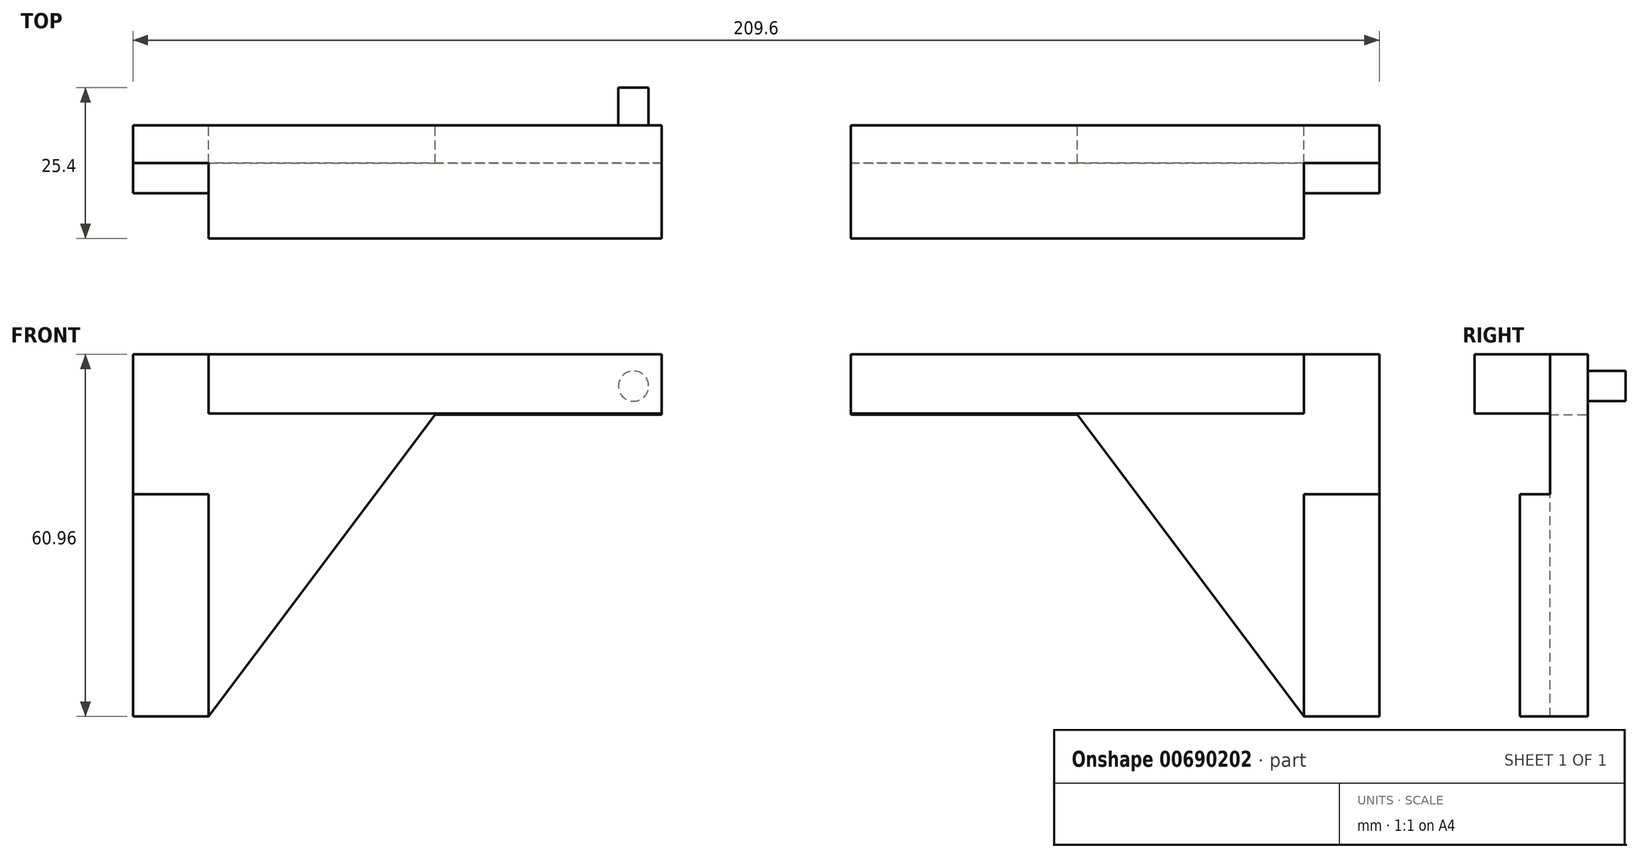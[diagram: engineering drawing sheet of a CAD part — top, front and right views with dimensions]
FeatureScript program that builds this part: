
annotation { "Feature Type Name" : "Feature", "Feature Type Description" : "" }
export const myFeature = defineFeature(function(context is Context, id is Id, definition is map)
    precondition{}
    {
        {
            var Q0;
            Q0=qCreatedBy(makeId("Front.planeOp"),FACE);
            var sketch = newSketch(context, id + "F0", { "sketchPlane" : qUnion([Q0])});
            skLineSegment(sketch, "E0.bottom", {"start": v(-92.1, -0.08) * mm, "end": v(-104.8, -0.08) * mm});
            skLineSegment(sketch, "E0.top", {"start": v(-92.1, 60.88) * mm, "end": v(-104.8, 60.88) * mm});
            skLineSegment(sketch, "E0.left", {"start": v(-92.1, -0.08) * mm, "end": v(-92.1, 60.88) * mm});
            skLineSegment(sketch, "E0.right", {"start": v(-104.8, -0.08) * mm, "end": v(-104.8, 60.88) * mm});
            skPoint(sketch, "E0.middle", {"position": v(-98.45, 30.4) * mm});
            skLineSegment(sketch, "E1", {"start": v(-92.1, 60.88) * mm, "end": v(-15.9, 60.88) * mm});
            skLineSegment(sketch, "E2.0", {"start": v(-92.1, 50.72) * mm, "end": v(-15.9, 50.72) * mm});
            skLineSegment(sketch, "E3", {"start": v(-15.9, 60.88) * mm, "end": v(-15.9, 50.72) * mm});
            skLineSegment(sketch, "E4", {"start": v(-92.1, -0.08) * mm, "end": v(-54, 50.72) * mm});
            skSolve(sketch);
        }
        {
            var Q0;
            Q0 = qSketchRegion(id + "F0", true);
            extrude(context, id + "F1", {"entities" : qUnion([Q0]), "depth" : 6.35 * mm, "offsetDistance" : 25.4 * mm});
        }
        {
            var Q0;
            Q0=makeQuery(id+"F1.opExtrude","CAP_FACE",FACE,{"disambiguationData":[OSD([sQuery(id+"F0.wireOp",EDGE,"E0.bottom"),sQuery(id+"F0.wireOp",EDGE,"E0.top"),sQuery(id+"F0.wireOp",EDGE,"E0.right"),sQuery(id+"F0.wireOp",EDGE,"E1"),sQuery(id+"F0.wireOp",EDGE,"E2.0"),sQuery(id+"F0.wireOp",EDGE,"E3"),sQuery(id+"F0.wireOp",EDGE,"E4")])],"isStart":false});
            var sketch = newSketch(context, id + "F2", { "sketchPlane" : qUnion([Q0])});
            skLineSegment(sketch, "E5.bottom", {"start": v(-104.8, -0.08) * mm, "end": v(-92.1, -0.08) * mm});
            skLineSegment(sketch, "E5.top", {"start": v(-104.8, 37.36) * mm, "end": v(-92.1, 37.36) * mm});
            skLineSegment(sketch, "E5.left", {"start": v(-104.8, -0.08) * mm, "end": v(-104.8, 37.36) * mm});
            skLineSegment(sketch, "E5.right", {"start": v(-92.1, -0.08) * mm, "end": v(-92.1, 37.36) * mm});
            skSolve(sketch);
        }
        {
            var Q0;
            Q0=makeQuery(id+"F2.imprint","IMPRINT",FACE,{"disambiguationData":[TD([[makeQuery(id+"F2.imprint","IMPRINT",EDGE,{"derivedFrom":sQuery(id+"F2.wireOp",EDGE,"E5.bottom")}),-1.0]])]});
            extrude(context, id + "F3", {"entities" : qUnion([Q0]), "operationType" : NewBodyOperationType.ADD, "depth" : 5.08 * mm, "offsetDistance" : 25.4 * mm});
        }
        {
            var Q0;
            {var subQ5=sQuery(id+"F0.wireOp",EDGE,"E1");Q0=makeQuery(id+"F0.imprint","IMPRINT",FACE,{"disambiguationData":[TD([[makeQuery(id+"F0.imprint","IMPRINT",EDGE,{"derivedFrom":subQ5}),-1.0]])]});}
            var sketch = newSketch(context, id + "F4", { "sketchPlane" : qUnion([Q0])});
            skCircle(sketch, "E6", {"center": v(-20.63, 55.53) * mm, "radius": 2.54 * mm});
            skSolve(sketch);
        }
        {
            var Q0;
            Q0=makeQuery(id+"F4.imprint","IMPRINT",FACE,{"disambiguationData":[TD([[makeQuery(id+"F4.imprint","IMPRINT",EDGE,{"derivedFrom":sQuery(id+"F4.wireOp",EDGE,"E6")}),1.0]])]});
            var Q1;
            Q1=sQuery(id+"F4.wireOp",EDGE,"E6");
            extrude(context, id + "F5", {"entities" : qUnion([Q0]), "surfaceEntities" : qUnion([Q1]), "oppositeDirection" : true, "depth" : 6.35 * mm, "offsetDistance" : 25.4 * mm});
        }
        {
            var Q0;
            Q0=makeQuery(id+"F1.opExtrude","SWEPT_BODY",BODY,{"disambiguationData":[OSD([sQuery(id+"F0.wireOp",EDGE,"E0.bottom"),sQuery(id+"F0.wireOp",EDGE,"E0.top"),sQuery(id+"F0.wireOp",EDGE,"E0.right"),sQuery(id+"F0.wireOp",EDGE,"E1"),sQuery(id+"F0.wireOp",EDGE,"E2.0"),sQuery(id+"F0.wireOp",EDGE,"E3"),sQuery(id+"F0.wireOp",EDGE,"E4")])]});
            transform(context, id + "F6", {"entities" : qUnion([Q0]), "transformType" : TransformType.TRANSLATION_3D, "dx" : 163.83 * mm, "dy" : -4.57 * mm, "dz" : -13.72 * mm, "makeCopy" : true});
        }
        {
            var Q0;
            Q0=makeQuery(id+"F6.opPattern","COPY",BODY,{"derivedFrom":makeQuery(id+"F1.opExtrude","SWEPT_BODY",BODY,{"disambiguationData":[OSD([sQuery(id+"F0.wireOp",EDGE,"E0.bottom"),sQuery(id+"F0.wireOp",EDGE,"E0.top"),sQuery(id+"F0.wireOp",EDGE,"E0.right"),sQuery(id+"F0.wireOp",EDGE,"E1"),sQuery(id+"F0.wireOp",EDGE,"E2.0"),sQuery(id+"F0.wireOp",EDGE,"E3"),sQuery(id+"F0.wireOp",EDGE,"E4")])]}),"instanceName":"1"});
            deleteBodies(context, id + "F7", {"entities" : qUnion([Q0])});
        }
        {
            var Q0;
            Q0=makeQuery(id+"F1.opExtrude","SWEPT_BODY",BODY,{"disambiguationData":[OSD([sQuery(id+"F0.wireOp",EDGE,"E0.bottom"),sQuery(id+"F0.wireOp",EDGE,"E0.top"),sQuery(id+"F0.wireOp",EDGE,"E0.right"),sQuery(id+"F0.wireOp",EDGE,"E1"),sQuery(id+"F0.wireOp",EDGE,"E2.0"),sQuery(id+"F0.wireOp",EDGE,"E3"),sQuery(id+"F0.wireOp",EDGE,"E4")])]});
            var Q1;
            Q1=makeQuery(id+"F1.opExtrude","SWEPT_EDGE",EDGE,{"disambiguationData":[OSD([sQuery(id+"F0.wireOp",EDGE,"E1"),sQuery(id+"F0.wireOp",EDGE,"E3")])]});
            transform(context, id + "F8", {"entities" : qUnion([Q0]), "transformType" : TransformType.TRANSLATION_3D, "dx" : 137.4 * mm, "dy" : 0 * mm, "dz" : 0 * mm, "makeCopy" : true});
        }
        {
            var Q0;
            Q0=makeQuery(id+"F8.opPattern","COPY",BODY,{"derivedFrom":makeQuery(id+"F1.opExtrude","SWEPT_BODY",BODY,{"disambiguationData":[OSD([sQuery(id+"F0.wireOp",EDGE,"E0.bottom"),sQuery(id+"F0.wireOp",EDGE,"E0.top"),sQuery(id+"F0.wireOp",EDGE,"E0.right"),sQuery(id+"F0.wireOp",EDGE,"E1"),sQuery(id+"F0.wireOp",EDGE,"E2.0"),sQuery(id+"F0.wireOp",EDGE,"E3"),sQuery(id+"F0.wireOp",EDGE,"E4")])]}),"instanceName":"1"});
            var Q1;
            Q1=makeQuery(id+"F8.opPattern","COPY",EDGE,{"derivedFrom":makeQuery(id+"F1.opExtrude","SWEPT_EDGE",EDGE,{"disambiguationData":[OSD([sQuery(id+"F0.wireOp",EDGE,"E1"),sQuery(id+"F0.wireOp",EDGE,"E3")])]}),"instanceName":"1"});
            transform(context, id + "F9", {"entities" : qUnion([Q0]), "transformType" : TransformType.ROTATION, "transformAxis" : qUnion([Q1]), "angle" : 180 * degree, "makeCopy" : true});
        }
        {
            var Q0;
            Q0=makeQuery(id+"F8.opPattern","COPY",BODY,{"derivedFrom":makeQuery(id+"F1.opExtrude","SWEPT_BODY",BODY,{"disambiguationData":[OSD([sQuery(id+"F0.wireOp",EDGE,"E0.bottom"),sQuery(id+"F0.wireOp",EDGE,"E0.top"),sQuery(id+"F0.wireOp",EDGE,"E0.right"),sQuery(id+"F0.wireOp",EDGE,"E1"),sQuery(id+"F0.wireOp",EDGE,"E2.0"),sQuery(id+"F0.wireOp",EDGE,"E3"),sQuery(id+"F0.wireOp",EDGE,"E4")])]}),"instanceName":"1"});
            deleteBodies(context, id + "F10", {"entities" : qUnion([Q0])});
        }
        {
            var Q0;
            Q0=makeQuery(id+"F1.opExtrude","SWEPT_BODY",BODY,{"disambiguationData":[OSD([sQuery(id+"F0.wireOp",EDGE,"E0.bottom"),sQuery(id+"F0.wireOp",EDGE,"E0.top"),sQuery(id+"F0.wireOp",EDGE,"E0.right"),sQuery(id+"F0.wireOp",EDGE,"E1"),sQuery(id+"F0.wireOp",EDGE,"E2.0"),sQuery(id+"F0.wireOp",EDGE,"E3"),sQuery(id+"F0.wireOp",EDGE,"E4")])]});
            var Q1;
            Q1=qCreatedBy(makeId("Right.planeOp"),FACE);
            mirror(context, id + "F11", {"entities" : qUnion([Q0]), "mirrorPlane" : qUnion([Q1])});
        }
        {
            var Q0;
            Q0=makeQuery(id+"F9.opPattern","COPY",BODY,{"derivedFrom":makeQuery(id+"F8.opPattern","COPY",BODY,{"derivedFrom":makeQuery(id+"F1.opExtrude","SWEPT_BODY",BODY,{"disambiguationData":[OSD([sQuery(id+"F0.wireOp",EDGE,"E0.bottom"),sQuery(id+"F0.wireOp",EDGE,"E0.top"),sQuery(id+"F0.wireOp",EDGE,"E0.right"),sQuery(id+"F0.wireOp",EDGE,"E1"),sQuery(id+"F0.wireOp",EDGE,"E2.0"),sQuery(id+"F0.wireOp",EDGE,"E3"),sQuery(id+"F0.wireOp",EDGE,"E4")])]}),"instanceName":"1"}),"instanceName":"1"});
            deleteBodies(context, id + "F12", {"entities" : qUnion([Q0])});
        }
        {
            var Q0;
            Q0=makeQuery(id+"F1.opExtrude","CAP_FACE",FACE,{"disambiguationData":[OSD([sQuery(id+"F0.wireOp",EDGE,"E0.bottom"),sQuery(id+"F0.wireOp",EDGE,"E0.top"),sQuery(id+"F0.wireOp",EDGE,"E0.right"),sQuery(id+"F0.wireOp",EDGE,"E1"),sQuery(id+"F0.wireOp",EDGE,"E2.0"),sQuery(id+"F0.wireOp",EDGE,"E3"),sQuery(id+"F0.wireOp",EDGE,"E4")])],"isStart":false});
            var sketch = newSketch(context, id + "F13", { "sketchPlane" : qUnion([Q0])});
            skLineSegment(sketch, "E7.bottom", {"start": v(-15.9, 60.88) * mm, "end": v(-92.1, 60.88) * mm});
            skLineSegment(sketch, "E7.top", {"start": v(-15.9, 50.88) * mm, "end": v(-92.1, 50.88) * mm});
            skLineSegment(sketch, "E7.left", {"start": v(-15.9, 60.88) * mm, "end": v(-15.9, 50.88) * mm});
            skLineSegment(sketch, "E7.right", {"start": v(-92.1, 60.88) * mm, "end": v(-92.1, 50.88) * mm});
            skSolve(sketch);
        }
        {
            var Q0;
            Q0=makeQuery(id+"F13.imprint","IMPRINT",FACE,{"disambiguationData":[TD([[makeQuery(id+"F13.imprint","IMPRINT",EDGE,{"derivedFrom":sQuery(id+"F13.wireOp",EDGE,"E7.bottom")}),1.0]])]});
            extrude(context, id + "F14", {"entities" : qUnion([Q0]), "operationType" : NewBodyOperationType.ADD, "depth" : 12.7 * mm, "offsetDistance" : 25.4 * mm});
        }
        {
            var Q0;
            Q0=makeQuery(id+"F11.opPattern","COPY",BODY,{"derivedFrom":makeQuery(id+"F1.opExtrude","SWEPT_BODY",BODY,{"disambiguationData":[OSD([sQuery(id+"F0.wireOp",EDGE,"E0.bottom"),sQuery(id+"F0.wireOp",EDGE,"E0.top"),sQuery(id+"F0.wireOp",EDGE,"E0.right"),sQuery(id+"F0.wireOp",EDGE,"E1"),sQuery(id+"F0.wireOp",EDGE,"E2.0"),sQuery(id+"F0.wireOp",EDGE,"E3"),sQuery(id+"F0.wireOp",EDGE,"E4")])]}),"instanceName":"1"});
            deleteBodies(context, id + "F15", {"entities" : qUnion([Q0])});
        }
        {
            var Q0;
            Q0=makeQuery(id+"F1.opExtrude","SWEPT_BODY",BODY,{"disambiguationData":[OSD([sQuery(id+"F0.wireOp",EDGE,"E0.bottom"),sQuery(id+"F0.wireOp",EDGE,"E0.top"),sQuery(id+"F0.wireOp",EDGE,"E0.right"),sQuery(id+"F0.wireOp",EDGE,"E1"),sQuery(id+"F0.wireOp",EDGE,"E2.0"),sQuery(id+"F0.wireOp",EDGE,"E3"),sQuery(id+"F0.wireOp",EDGE,"E4")])]});
            var Q1;
            Q1=qCreatedBy(makeId("Right.planeOp"),FACE);
            mirror(context, id + "F16", {"entities" : qUnion([Q0]), "mirrorPlane" : qUnion([Q1])});
        }
    });
